# Revit family: BathtubMixer-FromFloor-WithHandshower-Vitra-OriginSeries-A42681
name_source: partatom
category: Plumbing Fixtures
revit_build: Autodesk Revit 2017 (Build: 20160225_1515(x64)
units: mm (PartAtom-declared; Revit-internal decimal feet)

## family parameters
Cut with Voids When Loaded = No
Host = Face
OmniClass Number = 23.45.55.17
OmniClass Title = Mixing Faucets
Part Type = Normal
Room Calculation Point = No
Round Connector Dimension = Use Diameter
Shared = Yes

## types (1)
- BathtubMixer-FromFloor-WithHandshower-Vitra-OriginSeries-A42681
    Article No. (default) = A42681
    BIMobject category = Bath/Shower Mixer
    Brand = Vitra
    CW Connection = Yes
    Coating Material = Chrome
    Color = Chrome
    Connection Diameter (mm) = 15 mm  [stored 0.0492126 ft]
    Default Elevation = 0 mm  [stored 0 ft]
    Description = Origin From floor Bathtub Mixer
    Design country = Turkey
    HW Connection = Yes
    Hot Water Supply (max.) = 80 °C
    Hot Water temperature, factory set to = 38 °C
    IFC Classification = Sanitary Terminal
    Main Material = Brass
    Manufacturer = Vitra
    Manufacturer name = Vitra
    Masterformat 2014 Code = 22 40 00
    Masterformat 2014 Description = Plumbing Fixtures
    Min. flow pressure of = 0.5 bar
    Model = A42681
    Mounting type = From Floor
    NBS Referans Code = 45-35-70/315
    NBS Referans Description = Water supply fittings for baths
    Nominal Depth (mm) = 250 mm
    Nominal Height (mm) = 1070 mm  [stored 3.5105 ft]
    Nominal Width (mm) = 150 mm
    Number Of Connections = 2
    OmniClass Code = 23.45.55.17
    OmniClass Description = Mixing Faucets
    Product Properties = Bathtub Faucet
    Product SKU = A42681
    Product Type = Bathtub Mixer
    Product certification = https://www.vitraglobal.com
    Product family = Origin Bathtub Mixer
    Product group = Bathtub Mixer
    Product url = https://vitraglobal.com
    Range of Hot Water Supply = 5 - 65 °C
    Range of flow pressure = 1 - 5 bar
    Technical description = https://vitraglobal.com
    Test Pressure = 16 bar
    URL = https://vitraglobal.com
    Uniclass 1.4 Code = L725111
    Uniclass 1.4 Description = Mixer taps
    Uniclass 2.0 Code = Pr_40_20_87_09
    Uniclass 2.0 Description = Bath taps
    Uniclass 2015 Code = Pr_40_20_87_09
    Uniclass 2015 Name = Bath taps
    Uniformat II Code = 22 40 00
    Uniformat II Description = Plumbing Fixture
    Vent Connection = No
    Warranty Period (Year) = 10 Years
    Waste Connection = No
    Weight Net (kg) = 9.5
    Youtube = https://www.youtube.com

note: [stored X ft] marks values corroborated as IEEE doubles in the binary element streams (Revit-internal decimal feet)

## geometry (parser evidence)
native form markers: Sweep x2
no freeform markers — native parametric forms only
